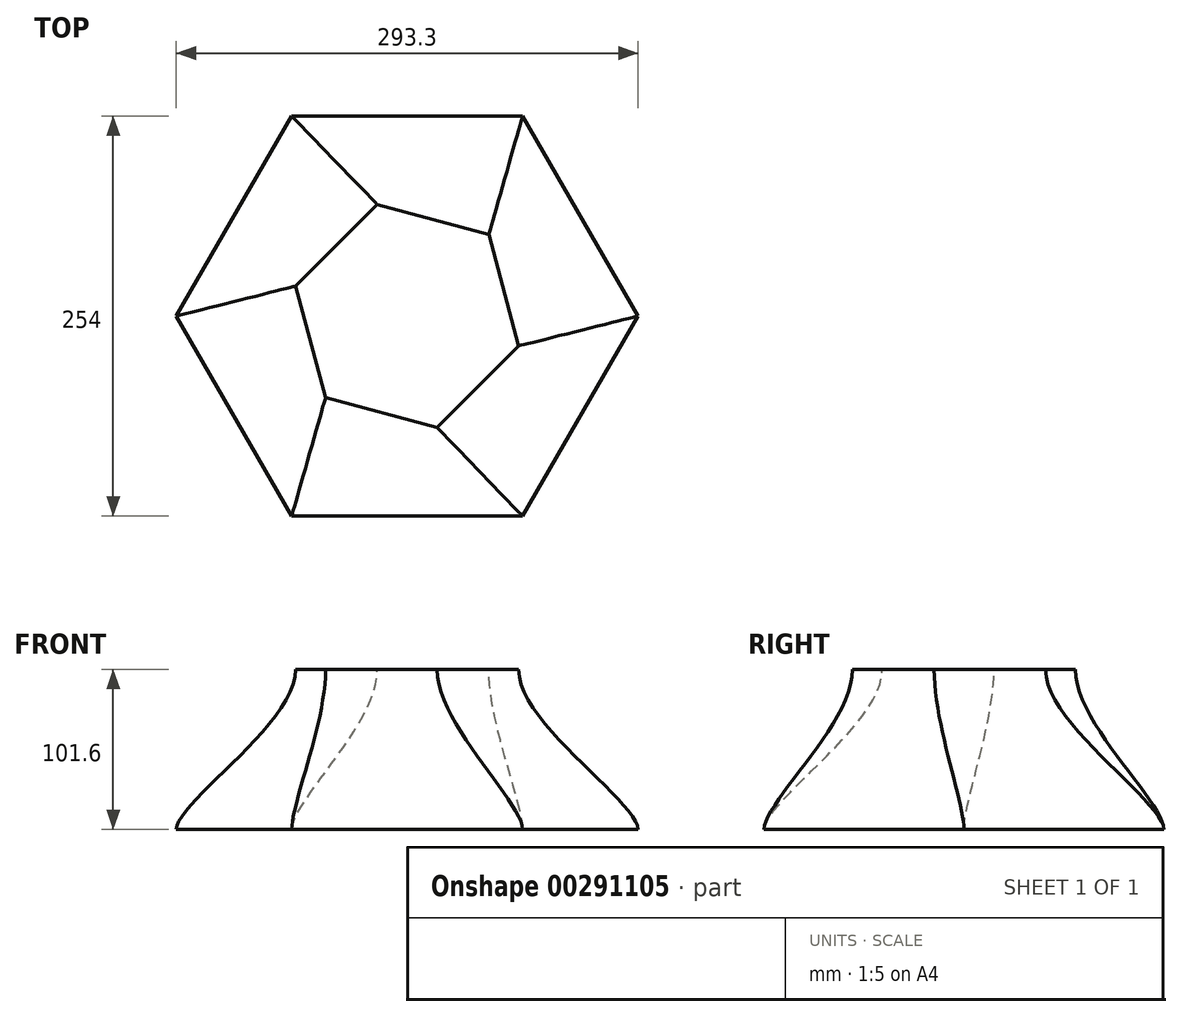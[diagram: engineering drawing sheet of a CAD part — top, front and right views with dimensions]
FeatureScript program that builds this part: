
annotation { "Feature Type Name" : "Feature", "Feature Type Description" : "" }
export const myFeature = defineFeature(function(context is Context, id is Id, definition is map)
    precondition{}
    {
        {
            var Q0;
            Q0=qCreatedBy(makeId("Top.planeOp"),FACE);
            var sketch = newSketch(context, id + "F0", { "sketchPlane" : qUnion([Q0])});
            skCircle(sketch, "E0.cCircle", {"center": v(0, 0) * mm, "radius": 127 * mm, "construction": true});
            skLineSegment(sketch, "E0.0", {"start": v(-73.32, 127) * mm, "end": v(73.32, 127) * mm});
            skLineSegment(sketch, "E0.1", {"start": v(73.32, 127) * mm, "end": v(146.65, 0) * mm});
            skLineSegment(sketch, "E0.2", {"start": v(146.65, 0) * mm, "end": v(73.32, -127) * mm});
            skLineSegment(sketch, "E0.3", {"start": v(73.32, -127) * mm, "end": v(-73.32, -127) * mm});
            skLineSegment(sketch, "E0.4", {"start": v(-73.32, -127) * mm, "end": v(-146.65, 0) * mm});
            skLineSegment(sketch, "E0.5", {"start": v(-146.65, 0) * mm, "end": v(-73.32, 127) * mm});
            skPoint(sketch, "E0.0.midPoint", {"position": v(0, 127) * mm});
            skSolve(sketch);
        }
        {
            var Q0;
            Q0=makeQuery(id+"F0.imprint","IMPRINT",FACE,{"disambiguationData":[TD([[makeQuery(id+"F0.imprint","IMPRINT",EDGE,{"derivedFrom":sQuery(id+"F0.wireOp",EDGE,"E0.0")}),-1.0]])]});
            cPlane(context, id + "F1", {"entities" : qUnion([Q0]), "cplaneType" : CPlaneType.OFFSET, "offset" : 101.6 * mm, "width" : 152.4 * mm, "height" : 152.4 * mm});
        }
        {
            var Q0;
            Q0=qCreatedBy(id+"F1.planeOp",FACE);
            var sketch = newSketch(context, id + "F2", { "sketchPlane" : qUnion([Q0])});
            skCircle(sketch, "E1.cCircle", {"center": v(0, 0) * mm, "radius": 63.5 * mm, "construction": true});
            skLineSegment(sketch, "E1.0", {"start": v(-51.85, -51.85) * mm, "end": v(-70.83, 18.98) * mm});
            skLineSegment(sketch, "E1.1", {"start": v(-70.83, 18.98) * mm, "end": v(-18.98, 70.83) * mm});
            skLineSegment(sketch, "E1.2", {"start": v(-18.98, 70.83) * mm, "end": v(51.85, 51.85) * mm});
            skLineSegment(sketch, "E1.3", {"start": v(51.85, 51.85) * mm, "end": v(70.83, -18.98) * mm});
            skLineSegment(sketch, "E1.4", {"start": v(70.83, -18.98) * mm, "end": v(18.98, -70.83) * mm});
            skLineSegment(sketch, "E1.5", {"start": v(18.98, -70.83) * mm, "end": v(-51.85, -51.85) * mm});
            skPoint(sketch, "E1.0.midPoint", {"position": v(-63.5, 0) * mm});
            skSolve(sketch);
        }
        {
            var Q0;
            Q0=makeQuery(id+"F0.imprint","IMPRINT",FACE,{"disambiguationData":[TD([[makeQuery(id+"F0.imprint","IMPRINT",EDGE,{"derivedFrom":sQuery(id+"F0.wireOp",EDGE,"E0.0")}),-1.0]])]});
            var Q1;
            Q1=makeQuery(id+"F2.imprint","IMPRINT",FACE,{"disambiguationData":[TD([[makeQuery(id+"F2.imprint","IMPRINT",EDGE,{"derivedFrom":sQuery(id+"F2.wireOp",EDGE,"E1.0")}),-1.0]])]});
            loft(context, id + "F3", {"startCondition" : LoftEndDerivativeType.NORMAL_TO_PROFILE, "startMagnitude" : .5, "endCondition" : LoftEndDerivativeType.NORMAL_TO_PROFILE, "endMagnitude" : 1, "sheetProfilesArray" : [{ "sheetProfileEntities" : qUnion([Q0]) }, { "sheetProfileEntities" : qUnion([Q1]) }]});
        }
    });
